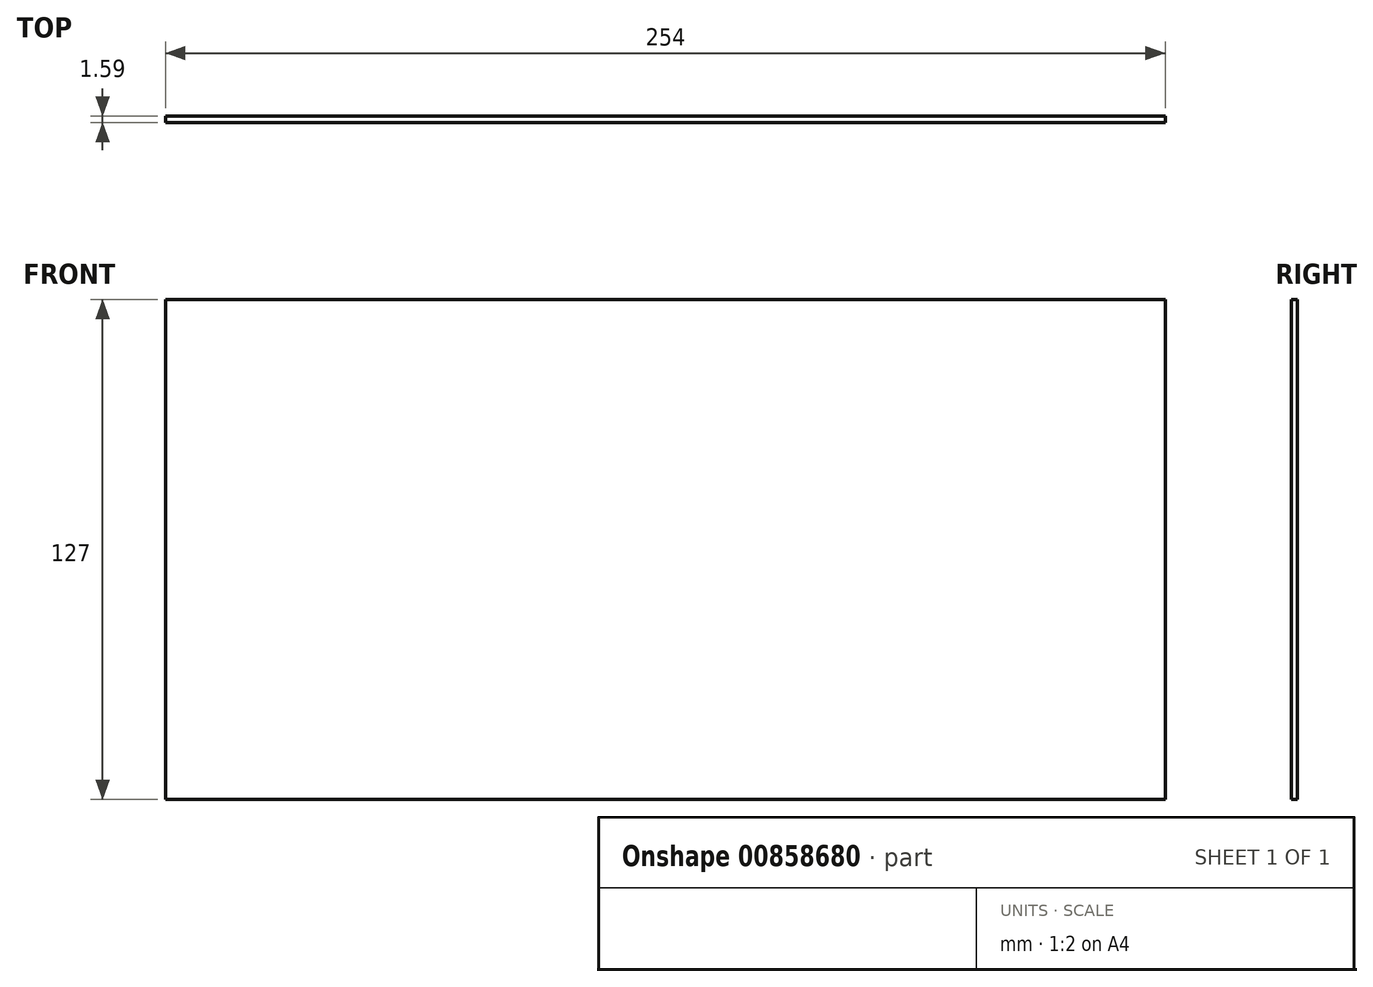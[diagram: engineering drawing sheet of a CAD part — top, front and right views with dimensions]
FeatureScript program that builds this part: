
annotation { "Feature Type Name" : "Feature", "Feature Type Description" : "" }
export const myFeature = defineFeature(function(context is Context, id is Id, definition is map)
    precondition{}
    {
        {
            var Q0;
            Q0=qCreatedBy(makeId("Front.planeOp"),FACE);
            var sketch = newSketch(context, id + "F0", { "sketchPlane" : qUnion([Q0])});
            skLineSegment(sketch, "E0.bottom", {"start": v(0, 0) * mm, "end": v(254, 0) * mm});
            skLineSegment(sketch, "E0.top", {"start": v(0, 127) * mm, "end": v(254, 127) * mm});
            skLineSegment(sketch, "E0.left", {"start": v(0, 0) * mm, "end": v(0, 127) * mm});
            skLineSegment(sketch, "E0.right", {"start": v(254, 0) * mm, "end": v(254, 127) * mm});
            skSolve(sketch);
        }
        {
            var Q0;
            Q0=makeQuery(id+"F0.imprint","IMPRINT",FACE,{"disambiguationData":[TD([[makeQuery(id+"F0.imprint","IMPRINT",EDGE,{"derivedFrom":sQuery(id+"F0.wireOp",EDGE,"E0.bottom")}),1.0]])]});
            extrude(context, id + "F1", {"entities" : qUnion([Q0]), "depth" : 1.59 * mm, "offsetDistance" : 25.4 * mm});
        }
    });
